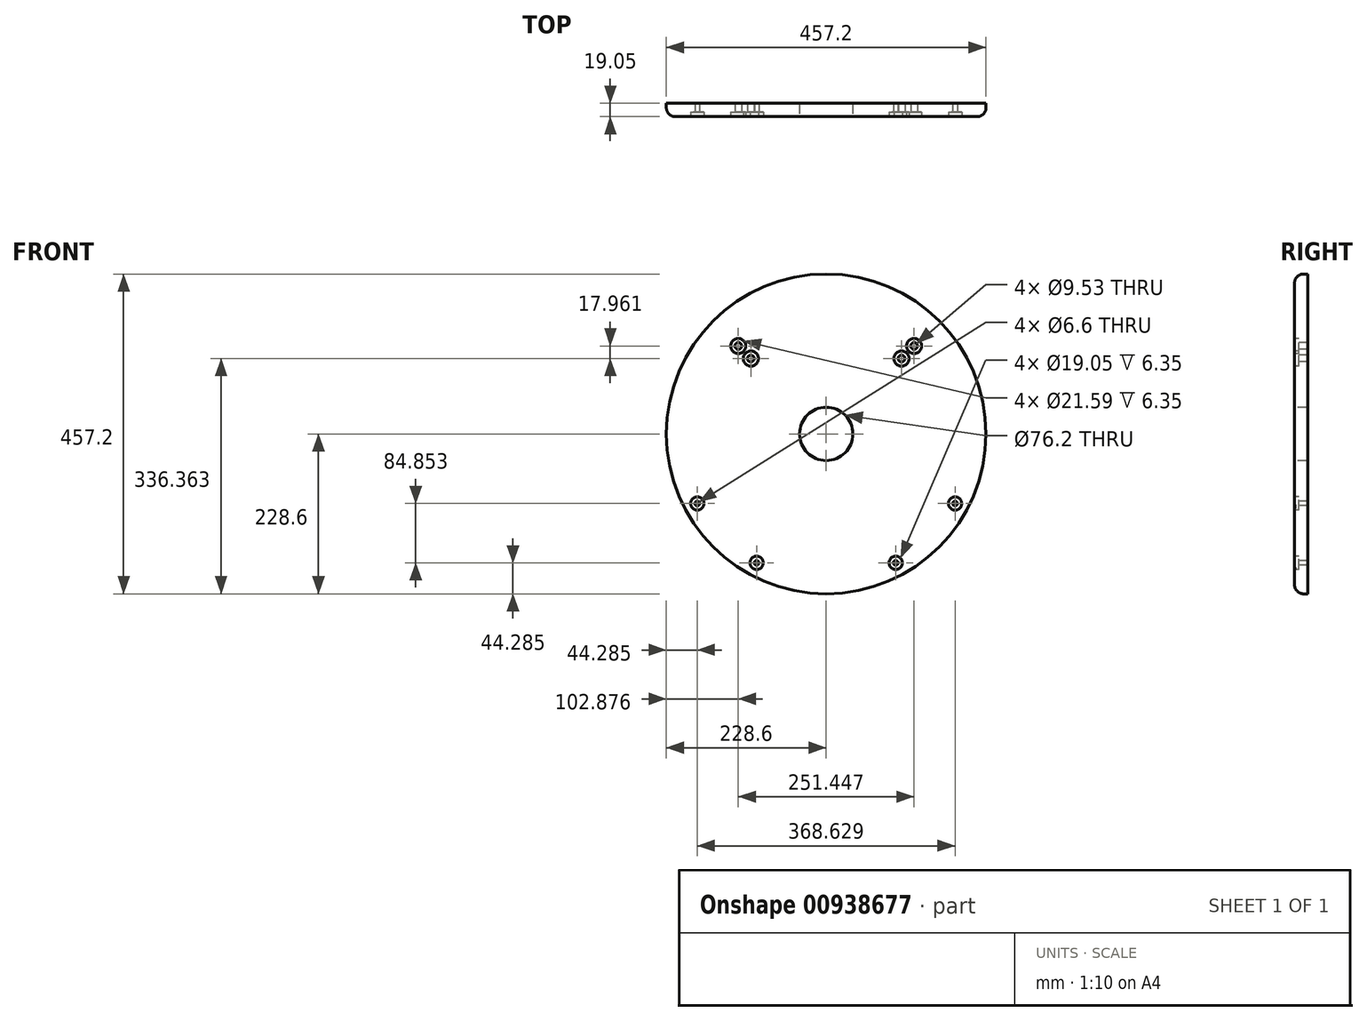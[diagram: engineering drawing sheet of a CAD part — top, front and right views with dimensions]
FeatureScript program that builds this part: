
annotation { "Feature Type Name" : "Feature", "Feature Type Description" : "" }
export const myFeature = defineFeature(function(context is Context, id is Id, definition is map)
    precondition{}
    {
        {
            var Q0;
            Q0=qCreatedBy(makeId("Front.planeOp"),FACE);
            var sketch = newSketch(context, id + "F0", { "sketchPlane" : qUnion([Q0])});
            skCircle(sketch, "E0", {"center": v(0, 0) * mm, "radius": 228.6 * mm});
            skSolve(sketch);
        }
        {
            var Q0;
            Q0=qSketchRegion(id+"F0",true);
            extrude(context, id + "F1", {"entities" : qUnion([Q0]), "depth" : 19.05 * mm, "offsetDistance" : 25.4 * mm});
        }
        {
            var Q0;
            Q0=makeQuery(id+"F1.opExtrude","CAP_FACE",FACE,{"disambiguationData":[OSD([sQuery(id+"F0.wireOp",EDGE,"E0")])],"isStart":false});
            var sketch = newSketch(context, id + "F2", { "sketchPlane" : qUnion([Q0])});
            skCircle(sketch, "E1", {"center": v(0, 0) * mm, "radius": 38.1 * mm});
            skSolve(sketch);
        }
        {
            var Q0;
            Q0=makeQuery(id+"F2.imprint","IMPRINT",FACE,{"disambiguationData":[TD([[makeQuery(id+"F2.imprint","IMPRINT",EDGE,{"derivedFrom":sQuery(id+"F2.wireOp",EDGE,"E1")}),1.0]])]});
            extrude(context, id + "F3", {"entities" : qUnion([Q0]), "operationType" : NewBodyOperationType.REMOVE, "endBound" : BoundingType.THROUGH_ALL, "oppositeDirection" : true, "depth" : 25.4 * mm, "offsetDistance" : 25.4 * mm});
        }
        {
            var Q0;
            Q0=makeQuery(id+"F1.opExtrude","CAP_FACE",FACE,{"disambiguationData":[OSD([sQuery(id+"F0.wireOp",EDGE,"E0")])],"isStart":false});
            var sketch = newSketch(context, id + "F4", { "sketchPlane" : qUnion([Q0])});
            skLineSegment(sketch, "E2", {"start": v(0, 0) * mm, "end": v(161.64, 161.64) * mm, "construction": true});
            skLineSegment(sketch, "E3", {"start": v(0, 0) * mm, "end": v(-161.64, 161.64) * mm, "construction": true});
            skLineSegment(sketch, "E4", {"start": v(-228.6, 0) * mm, "end": v(228.6, 0) * mm, "construction": true});
            skLineSegment(sketch, "E5", {"start": v(-161.64, 161.64) * mm, "end": v(-161.64, 0) * mm, "construction": true});
            skLineSegment(sketch, "E6", {"start": v(161.64, 161.64) * mm, "end": v(161.64, 0) * mm, "construction": true});
            skCircle(sketch, "E7", {"center": v(107.76, 107.76) * mm, "radius": 4.76 * mm});
            skCircle(sketch, "E8", {"center": v(125.72, 125.72) * mm, "radius": 4.76 * mm});
            skLineSegment(sketch, "E9", {"start": v(0, 0) * mm, "end": v(0, 228.6) * mm, "construction": true});
            skCircle(sketch, "E10.MirrorC", {"center": v(-107.76, 107.76) * mm, "radius": 4.76 * mm});
            skCircle(sketch, "E11.MirrorC", {"center": v(-125.72, 125.72) * mm, "radius": 4.76 * mm});
            skLineSegment(sketch, "E12", {"start": v(0, 0) * mm, "end": v(161.64, -161.64) * mm, "construction": true});
            skLineSegment(sketch, "E13", {"start": v(0, 0) * mm, "end": v(-161.64, -161.64) * mm, "construction": true});
            skLineSegment(sketch, "E14", {"start": v(0, 0) * mm, "end": v(0, -228.6) * mm, "construction": true});
            skCircle(sketch, "E15", {"center": v(-99.46, -184.31) * mm, "radius": 3.3 * mm});
            skCircle(sketch, "E16", {"center": v(-184.31, -99.46) * mm, "radius": 3.3 * mm});
            skLineSegment(sketch, "E17", {"start": v(-184.31, -99.46) * mm, "end": v(-141.89, -141.89) * mm, "construction": true});
            skLineSegment(sketch, "E18", {"start": v(-141.89, -141.89) * mm, "end": v(-99.46, -184.31) * mm, "construction": true});
            skCircle(sketch, "E19.MirrorC", {"center": v(99.46, -184.31) * mm, "radius": 3.3 * mm});
            skCircle(sketch, "E20.MirrorC", {"center": v(184.31, -99.46) * mm, "radius": 3.3 * mm});
            skSolve(sketch);
        }
        {
            var Q0;
            Q0=qSketchRegion(id+"F4",true);
            extrude(context, id + "F5", {"entities" : qUnion([Q0]), "operationType" : NewBodyOperationType.REMOVE, "endBound" : BoundingType.THROUGH_ALL, "oppositeDirection" : true, "depth" : 25.4 * mm, "offsetDistance" : 25.4 * mm});
        }
        {
            var Q0;
            Q0=makeQuery(id+"F1.opExtrude","CAP_FACE",FACE,{"disambiguationData":[OSD([sQuery(id+"F0.wireOp",EDGE,"E0")])],"isStart":false});
            var sketch = newSketch(context, id + "F6", { "sketchPlane" : qUnion([Q0])});
            skLineSegment(sketch, "E21", {"start": v(0, 0) * mm, "end": v(0, 228.6) * mm, "construction": true});
            skCircle(sketch, "E22", {"center": v(107.76, 107.76) * mm, "radius": 10.8 * mm});
            skCircle(sketch, "E23", {"center": v(125.72, 125.72) * mm, "radius": 10.8 * mm});
            skCircle(sketch, "E24.MirrorC", {"center": v(-125.72, 125.72) * mm, "radius": 10.8 * mm});
            skCircle(sketch, "E25.MirrorC", {"center": v(-107.76, 107.76) * mm, "radius": 10.8 * mm});
            skCircle(sketch, "E26", {"center": v(-184.31, -99.46) * mm, "radius": 9.53 * mm});
            skCircle(sketch, "E27", {"center": v(-99.46, -184.31) * mm, "radius": 9.53 * mm});
            skCircle(sketch, "E28", {"center": v(99.46, -184.31) * mm, "radius": 9.53 * mm});
            skCircle(sketch, "E29", {"center": v(184.31, -99.46) * mm, "radius": 9.53 * mm});
            skSolve(sketch);
        }
        {
            var Q0;
            Q0=qSketchRegion(id+"F6",true);
            extrude(context, id + "F7", {"entities" : qUnion([Q0]), "operationType" : NewBodyOperationType.REMOVE, "oppositeDirection" : true, "depth" : 6.35 * mm, "offsetDistance" : 25.4 * mm});
        }
        {
            var Q0;
            Q0=makeQuery(id+"F1.opExtrude","CAP_EDGE",EDGE,{"disambiguationData":[OSD([sQuery(id+"F0.wireOp",EDGE,"E0")])],"isStart":false});
            var Q1;
            Q1=makeQuery(id+"F3.boolean.opBoolean","COPY",EDGE,{"derivedFrom":makeQuery(id+"F3.opExtrude","CAP_EDGE",EDGE,{"disambiguationData":[OSD([sQuery(id+"F2.wireOp",EDGE,"E1")])],"isStart":true})});
            fillet(context, id + "F8", {"entities" : qUnion([Q0, Q1]), "radius" : 12.7 * mm, "tangentPropagation" : true, "allowEdgeOverflow" : false});
        }
    });
